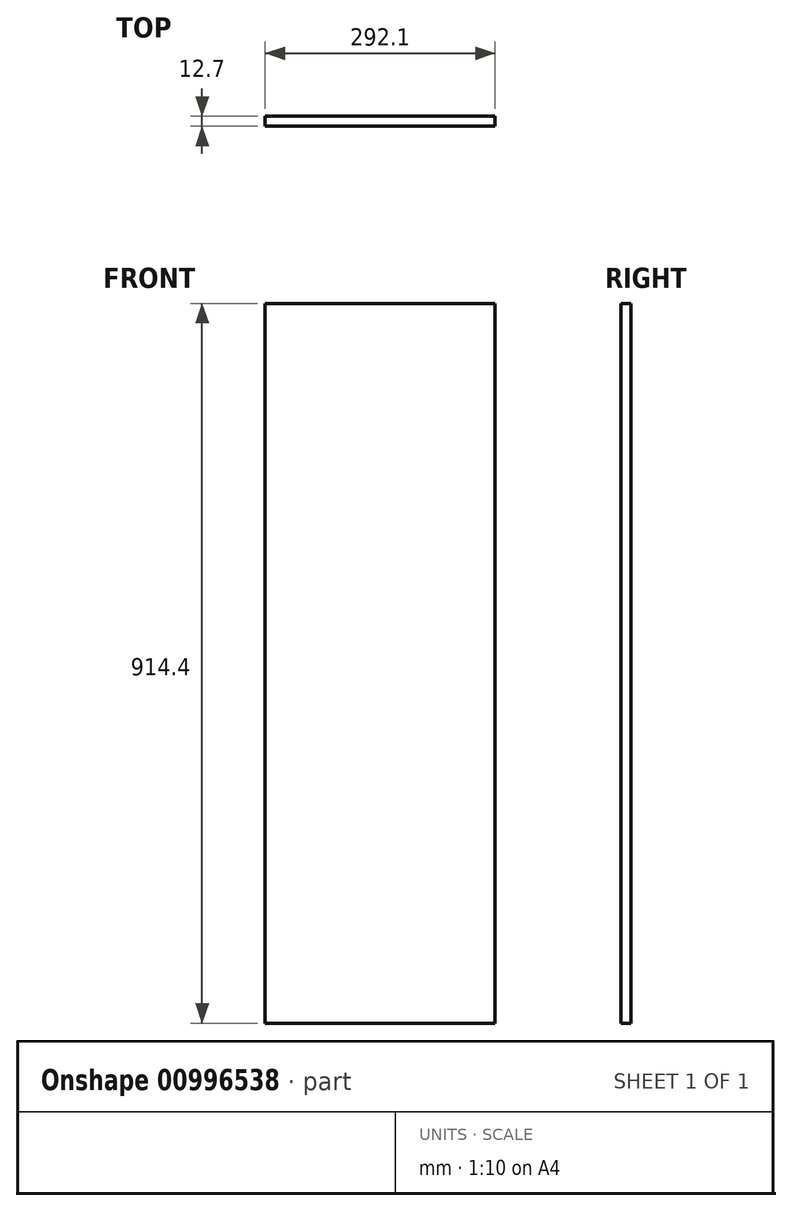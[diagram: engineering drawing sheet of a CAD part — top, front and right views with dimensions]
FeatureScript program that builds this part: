
annotation { "Feature Type Name" : "Feature", "Feature Type Description" : "" }
export const myFeature = defineFeature(function(context is Context, id is Id, definition is map)
    precondition{}
    {
        {
            var Q0;
            Q0=qCreatedBy(makeId("Front.planeOp"),FACE);
            var sketch = newSketch(context, id + "F0", { "sketchPlane" : qUnion([Q0])});
            skLineSegment(sketch, "E0.bottom", {"start": v(134.67, 696.93) * mm, "end": v(-157.43, 696.93) * mm});
            skLineSegment(sketch, "E0.top", {"start": v(134.67, -217.47) * mm, "end": v(-157.43, -217.47) * mm});
            skLineSegment(sketch, "E0.left", {"start": v(134.67, 696.93) * mm, "end": v(134.67, -217.47) * mm});
            skLineSegment(sketch, "E0.right", {"start": v(-157.43, 696.93) * mm, "end": v(-157.43, -217.47) * mm});
            skSolve(sketch);
        }
        {
            var Q0;
            Q0=makeQuery(id+"F0.imprint","IMPRINT",FACE,{"disambiguationData":[TD([[makeQuery(id+"F0.imprint","IMPRINT",EDGE,{"derivedFrom":sQuery(id+"F0.wireOp",EDGE,"E0.bottom")}),1.0]])]});
            extrude(context, id + "F1", {"entities" : qUnion([Q0]), "depth" : 12.7 * mm, "offsetDistance" : 25.4 * mm});
        }
    });
